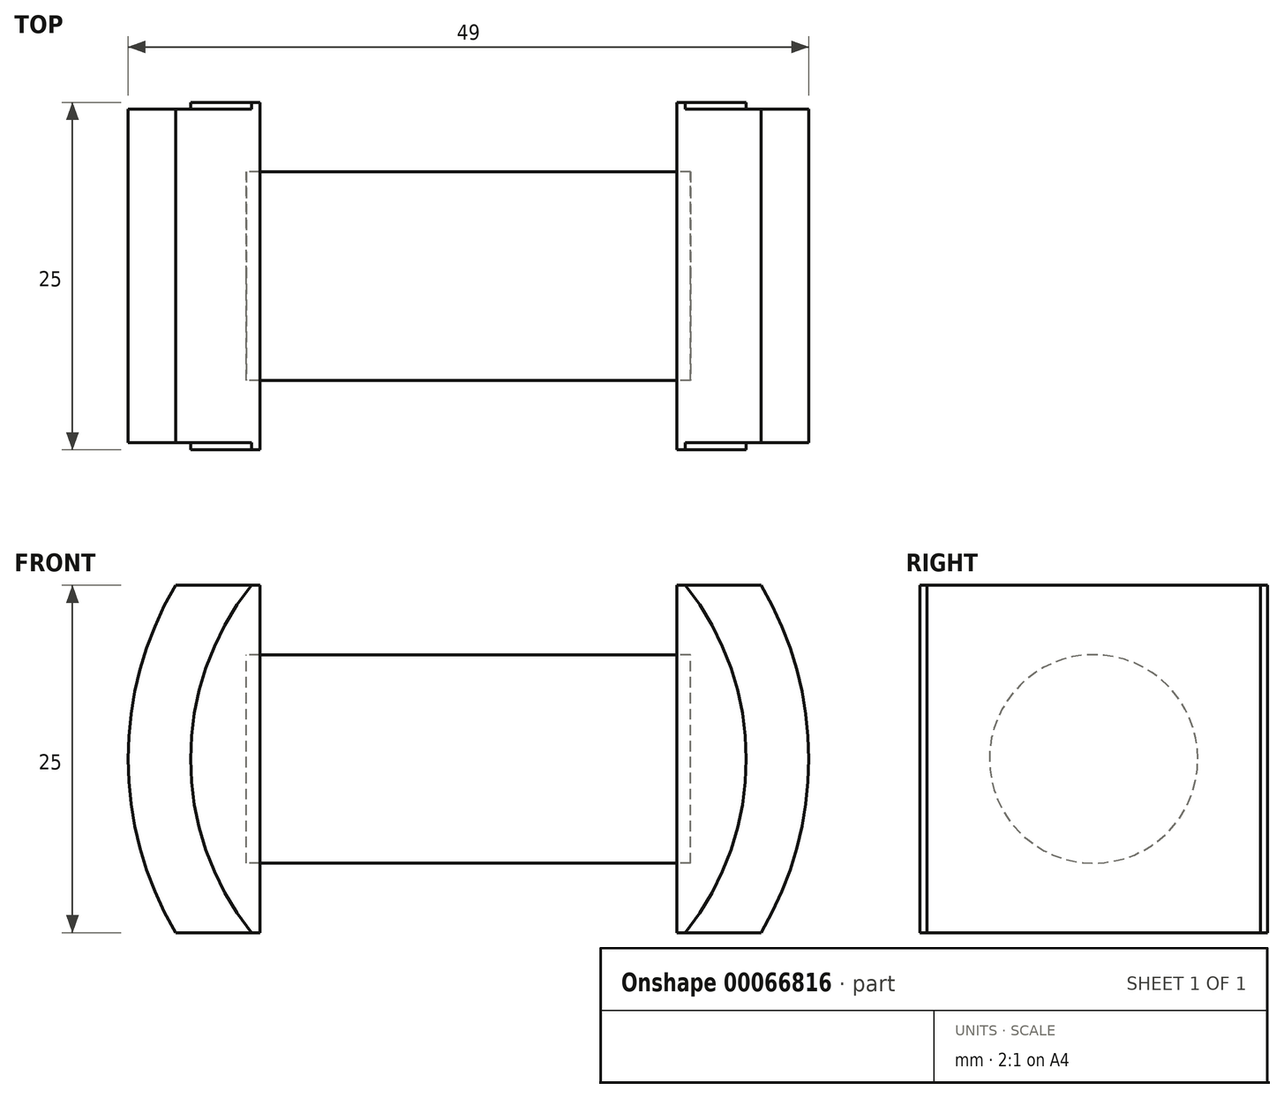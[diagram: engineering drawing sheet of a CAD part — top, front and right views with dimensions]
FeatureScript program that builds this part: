
annotation { "Feature Type Name" : "Feature", "Feature Type Description" : "" }
export const myFeature = defineFeature(function(context is Context, id is Id, definition is map)
    precondition{}
    {
        {
            var Q0;
            Q0=qCreatedBy(makeId("Right.planeOp"),FACE);
            var sketch = newSketch(context, id + "F0", { "sketchPlane" : qUnion([Q0])});
            skLineSegment(sketch, "E0.bottom", {"start": v(-12.5, 12.5) * mm, "end": v(12.5, 12.5) * mm});
            skLineSegment(sketch, "E0.top", {"start": v(-12.5, -12.5) * mm, "end": v(12.5, -12.5) * mm});
            skLineSegment(sketch, "E0.left", {"start": v(-12.5, 12.5) * mm, "end": v(-12.5, -12.5) * mm});
            skLineSegment(sketch, "E0.right", {"start": v(12.5, 12.5) * mm, "end": v(12.5, -12.5) * mm});
            skPoint(sketch, "E0.middle", {"position": v(0, 0) * mm});
            skCircle(sketch, "E1", {"center": v(0, 0) * mm, "radius": 7.5 * mm});
            skSolve(sketch);
        }
        {
            var Q0;
            Q0=makeQuery(id+"F0.imprint","IMPRINT",FACE,{"disambiguationData":[TD([[makeQuery(id+"F0.imprint","IMPRINT",EDGE,{"derivedFrom":sQuery(id+"F0.wireOp",EDGE,"E1")}),1.0]])]});
            var Q1;
            Q1=makeQuery(id+"F0.imprint","IMPRINT",FACE,{"disambiguationData":[TD([[makeQuery(id+"F0.imprint","IMPRINT",EDGE,{"derivedFrom":sQuery(id+"F0.wireOp",EDGE,"E0.bottom")}),-1.0]])]});
            extrude(context, id + "F1", {"entities" : qUnion([Q0, Q1]), "oppositeDirection" : true, "depth" : 25 * mm, "hasSecondDirection" : true, "secondDirectionOppositeDirection" : true, "secondDirectionDepth" : 15 * mm});
        }
        {
            var Q0;
            Q0=makeQuery(id+"F0.imprint","IMPRINT",FACE,{"disambiguationData":[TD([[makeQuery(id+"F0.imprint","IMPRINT",EDGE,{"derivedFrom":sQuery(id+"F0.wireOp",EDGE,"E0.bottom")}),-1.0]])]});
            var Q1;
            Q1=makeQuery(id+"F0.imprint","IMPRINT",FACE,{"disambiguationData":[TD([[makeQuery(id+"F0.imprint","IMPRINT",EDGE,{"derivedFrom":sQuery(id+"F0.wireOp",EDGE,"E1")}),1.0]])]});
            extrude(context, id + "F2", {"entities" : qUnion([Q0, Q1]), "depth" : 25 * mm, "hasSecondDirection" : true, "secondDirectionOppositeDirection" : false, "secondDirectionDepth" : 15 * mm});
        }
        {
            var Q0;
            Q0=makeQuery(id+"F0.imprint","IMPRINT",FACE,{"disambiguationData":[TD([[makeQuery(id+"F0.imprint","IMPRINT",EDGE,{"derivedFrom":sQuery(id+"F0.wireOp",EDGE,"E1")}),1.0]])]});
            extrude(context, id + "F3", {"entities" : qUnion([Q0]), "depth" : 16 * mm, "hasSecondDirection" : true, "secondDirectionOppositeDirection" : true, "secondDirectionDepth" : 16 * mm});
        }
        {
            var Q0;
            Q0=qCreatedBy(makeId("Front.planeOp"),FACE);
            var sketch = newSketch(context, id + "F4", { "sketchPlane" : qUnion([Q0])});
            skCircle(sketch, "E2", {"center": v(0, 0) * mm, "radius": 24.5 * mm});
            skSolve(sketch);
        }
        {
            var Q0;
            Q0=makeQuery(id+"F4.imprint","IMPRINT",FACE,{"disambiguationData":[TD([[makeQuery(id+"F4.imprint","IMPRINT",EDGE,{"derivedFrom":sQuery(id+"F4.wireOp",EDGE,"E2")}),1.0]])]});
            extrude(context, id + "F5", {"entities" : qUnion([Q0]), "operationType" : NewBodyOperationType.INTERSECT, "depth" : 25 * mm, "hasSecondDirection" : true, "secondDirectionOppositeDirection" : true, "secondDirectionDepth" : 25 * mm});
        }
        {
            var Q0;
            Q0=qCreatedBy(makeId("Front.planeOp"),FACE);
            var sketch = newSketch(context, id + "F6", { "sketchPlane" : qUnion([Q0])});
            skCircle(sketch, "E3", {"center": v(0, 0) * mm, "radius": 20 * mm});
            skCircle(sketch, "E4", {"center": v(0, 0) * mm, "radius": 37.88 * mm});
            skSolve(sketch);
        }
        {
            var Q0;
            Q0=makeQuery(id+"F6.imprint","IMPRINT",FACE,{"disambiguationData":[TD([[makeQuery(id+"F6.imprint","IMPRINT",EDGE,{"derivedFrom":sQuery(id+"F6.wireOp",EDGE,"E3")}),-1.0]])]});
            extrude(context, id + "F7", {"entities" : qUnion([Q0]), "operationType" : NewBodyOperationType.REMOVE, "oppositeDirection" : true, "depth" : 25 * mm, "hasSecondDirection" : true, "secondDirectionOppositeDirection" : true, "secondDirectionDepth" : 12 * mm});
        }
        {
            var Q0;
            Q0=makeQuery(id+"F6.imprint","IMPRINT",FACE,{"disambiguationData":[TD([[makeQuery(id+"F6.imprint","IMPRINT",EDGE,{"derivedFrom":sQuery(id+"F6.wireOp",EDGE,"E3")}),-1.0]])]});
            extrude(context, id + "F8", {"entities" : qUnion([Q0]), "operationType" : NewBodyOperationType.REMOVE, "depth" : 25 * mm, "hasSecondDirection" : true, "secondDirectionOppositeDirection" : false, "secondDirectionDepth" : 12 * mm});
        }
    });
